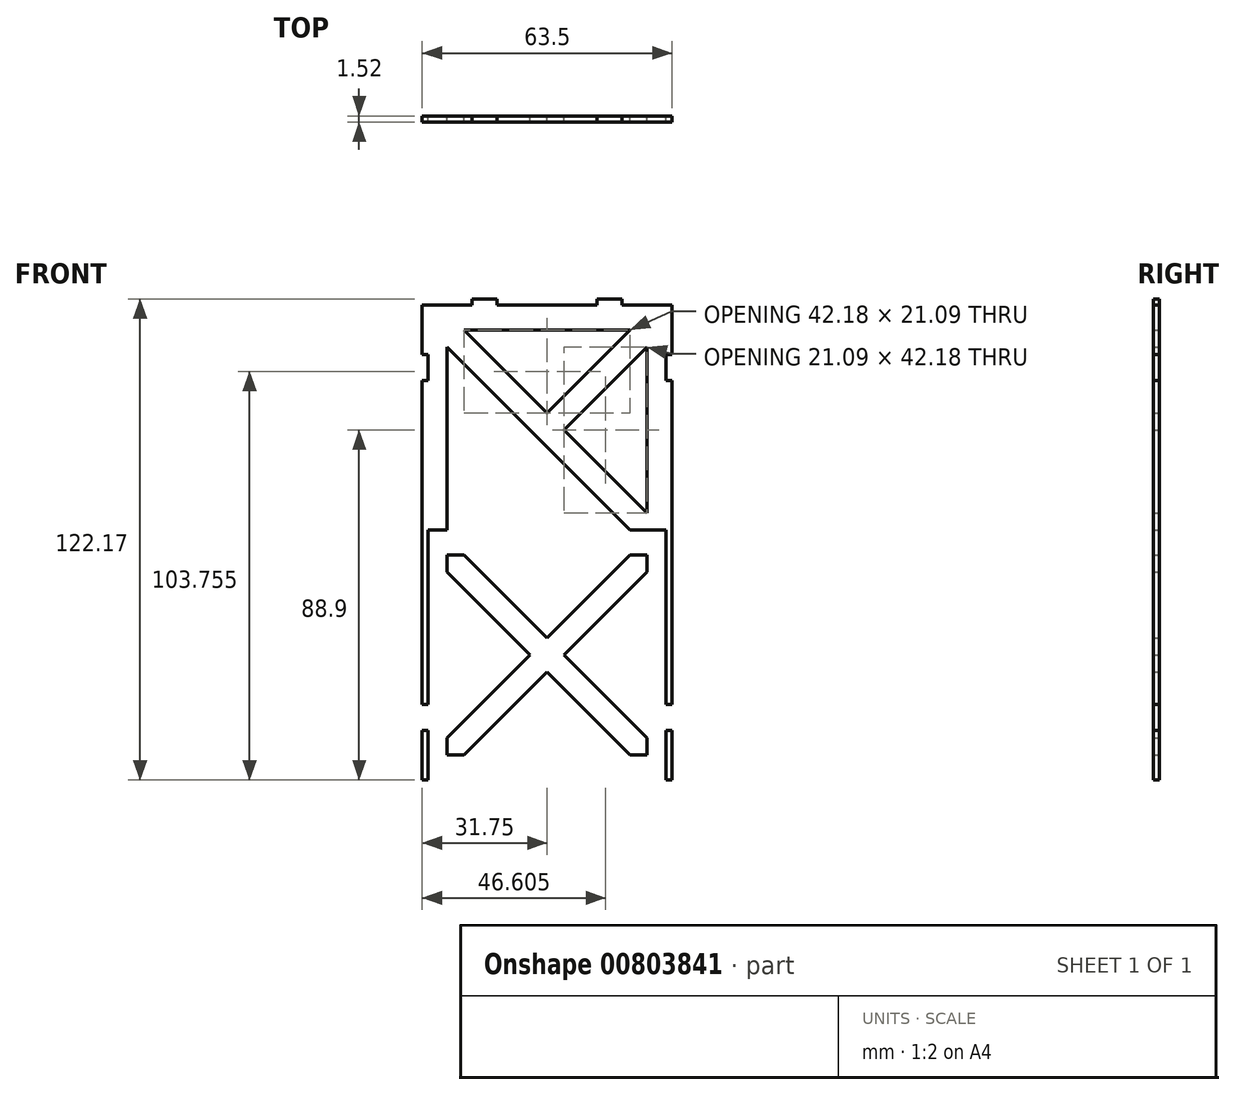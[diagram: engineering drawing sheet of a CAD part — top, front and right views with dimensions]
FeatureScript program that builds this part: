
annotation { "Feature Type Name" : "Feature", "Feature Type Description" : "" }
export const myFeature = defineFeature(function(context is Context, id is Id, definition is map)
    precondition{}
    {
        {
            var Q0;
            Q0=qCreatedBy(makeId("Front.planeOp"),FACE);
            var sketch = newSketch(context, id + "F0", { "sketchPlane" : qUnion([Q0])});
            skLineSegment(sketch, "E0.bottom", {"start": v(31.75, 31.75) * mm, "end": v(-31.75, 31.75) * mm});
            skLineSegment(sketch, "E0.top", {"start": v(31.75, -31.75) * mm, "end": v(-31.75, -31.75) * mm});
            skLineSegment(sketch, "E0.left", {"start": v(31.75, 31.75) * mm, "end": v(31.75, -31.75) * mm});
            skLineSegment(sketch, "E0.right", {"start": v(-31.75, 31.75) * mm, "end": v(-31.75, -31.75) * mm});
            skPoint(sketch, "E0.middle", {"position": v(0, 0) * mm});
            skLineSegment(sketch, "E1.bottom", {"start": v(-19.05, -31.75) * mm, "end": v(-12.7, -31.75) * mm});
            skLineSegment(sketch, "E1.top", {"start": v(-19.05, -33.27) * mm, "end": v(-12.7, -33.27) * mm});
            skLineSegment(sketch, "E1.left", {"start": v(-19.05, -31.75) * mm, "end": v(-19.05, -33.27) * mm});
            skLineSegment(sketch, "E1.right", {"start": v(-12.7, -31.75) * mm, "end": v(-12.7, -33.27) * mm});
            skPoint(sketch, "E2", {"position": v(-15.88, -31.75) * mm});
            skLineSegment(sketch, "E3.MirrorCS", {"start": v(19.05, -31.75) * mm, "end": v(12.7, -31.75) * mm});
            skPoint(sketch, "E4.MirrorP", {"position": v(15.88, -31.75) * mm});
            skLineSegment(sketch, "E5.MirrorCS", {"start": v(19.05, -33.27) * mm, "end": v(12.7, -33.27) * mm});
            skLineSegment(sketch, "E6.MirrorCS", {"start": v(12.7, -31.75) * mm, "end": v(12.7, -33.27) * mm});
            skLineSegment(sketch, "E7.MirrorCS", {"start": v(19.05, -31.75) * mm, "end": v(19.05, -33.27) * mm});
            skLineSegment(sketch, "E8.bottom", {"start": v(-31.75, -19.18) * mm, "end": v(-30.23, -19.18) * mm});
            skLineSegment(sketch, "E8.top", {"start": v(-31.75, -12.57) * mm, "end": v(-30.23, -12.57) * mm});
            skLineSegment(sketch, "E8.left", {"start": v(-31.75, -19.18) * mm, "end": v(-31.75, -12.57) * mm});
            skLineSegment(sketch, "E8.right", {"start": v(-30.23, -19.18) * mm, "end": v(-30.23, -12.57) * mm});
            skPoint(sketch, "E9", {"position": v(-31.75, -15.88) * mm});
            skLineSegment(sketch, "E10.MirrorCS", {"start": v(-31.75, 19.18) * mm, "end": v(-30.23, 19.18) * mm});
            skPoint(sketch, "E11.MirrorP", {"position": v(-31.75, 15.88) * mm});
            skLineSegment(sketch, "E12.MirrorCS", {"start": v(-31.75, 12.57) * mm, "end": v(-30.23, 12.57) * mm});
            skLineSegment(sketch, "E13.MirrorCS", {"start": v(-31.75, 19.18) * mm, "end": v(-31.75, 12.57) * mm});
            skLineSegment(sketch, "E14.MirrorCS", {"start": v(-30.23, 19.18) * mm, "end": v(-30.23, 12.57) * mm});
            skLineSegment(sketch, "E15.MirrorCS", {"start": v(31.75, 19.18) * mm, "end": v(30.23, 19.18) * mm});
            skLineSegment(sketch, "E16.MirrorCS", {"start": v(31.75, -19.18) * mm, "end": v(30.23, -19.18) * mm});
            skLineSegment(sketch, "E17.MirrorCS", {"start": v(31.75, -12.57) * mm, "end": v(30.23, -12.57) * mm});
            skLineSegment(sketch, "E18.MirrorCS", {"start": v(31.75, 12.57) * mm, "end": v(30.23, 12.57) * mm});
            skLineSegment(sketch, "E19.MirrorCS", {"start": v(30.23, 19.18) * mm, "end": v(30.23, 12.57) * mm});
            skLineSegment(sketch, "E20.MirrorCS", {"start": v(30.23, -19.18) * mm, "end": v(30.23, -12.57) * mm});
            skLineSegment(sketch, "E21.MirrorCS", {"start": v(31.75, 19.18) * mm, "end": v(31.75, 12.57) * mm});
            skLineSegment(sketch, "E22.MirrorCS", {"start": v(31.75, -19.18) * mm, "end": v(31.75, -12.57) * mm});
            skPoint(sketch, "E23.MirrorP", {"position": v(31.75, 15.88) * mm});
            skPoint(sketch, "E24.MirrorP", {"position": v(31.75, -15.88) * mm});
            skLineSegment(sketch, "E25.0", {"start": v(-30.23, 31.75) * mm, "end": v(-30.23, -31.75) * mm});
            skLineSegment(sketch, "E26.MirrorCS", {"start": v(30.23, 31.75) * mm, "end": v(30.23, -31.75) * mm});
            skLineSegment(sketch, "E27.bottom", {"start": v(25.4, 25.4) * mm, "end": v(-25.4, 25.4) * mm});
            skLineSegment(sketch, "E27.top", {"start": v(25.4, -25.4) * mm, "end": v(-25.4, -25.4) * mm});
            skLineSegment(sketch, "E27.left", {"start": v(25.4, 25.4) * mm, "end": v(25.4, -25.4) * mm});
            skLineSegment(sketch, "E27.right", {"start": v(-25.4, 25.4) * mm, "end": v(-25.4, -25.4) * mm});
            skLineSegment(sketch, "E28", {"start": v(-25.4, -25.4) * mm, "end": v(25.4, 25.4) * mm, "construction": true});
            skLineSegment(sketch, "E29", {"start": v(-25.4, 25.4) * mm, "end": v(25.4, -25.4) * mm, "construction": true});
            skLineSegment(sketch, "E30.0", {"start": v(-27.56, 23.24) * mm, "end": v(23.24, -27.56) * mm});
            skLineSegment(sketch, "E31.0", {"start": v(-23.24, 27.56) * mm, "end": v(27.56, -23.24) * mm});
            skLineSegment(sketch, "E32.0", {"start": v(-23.24, -27.56) * mm, "end": v(27.56, 23.24) * mm});
            skLineSegment(sketch, "E33.0", {"start": v(-27.56, -23.24) * mm, "end": v(23.24, 27.56) * mm});
            skLineSegment(sketch, "E34.MirrorCS", {"start": v(-19.05, 31.75) * mm, "end": v(-19.05, 33.27) * mm});
            skLineSegment(sketch, "E35.MirrorCS", {"start": v(-12.7, 31.75) * mm, "end": v(-12.7, 33.27) * mm});
            skLineSegment(sketch, "E36.MirrorCS", {"start": v(12.7, 31.75) * mm, "end": v(12.7, 33.27) * mm});
            skLineSegment(sketch, "E37.MirrorCS", {"start": v(19.05, 31.75) * mm, "end": v(19.05, 33.27) * mm});
            skLineSegment(sketch, "E38.MirrorCS", {"start": v(-19.05, 31.75) * mm, "end": v(-12.7, 31.75) * mm});
            skLineSegment(sketch, "E39.MirrorCS", {"start": v(-19.05, 33.27) * mm, "end": v(-12.7, 33.27) * mm});
            skLineSegment(sketch, "E40.MirrorCS", {"start": v(19.05, 31.75) * mm, "end": v(12.7, 31.75) * mm});
            skLineSegment(sketch, "E41.MirrorCS", {"start": v(19.05, 33.27) * mm, "end": v(12.7, 33.27) * mm});
            skPoint(sketch, "E42.MirrorP", {"position": v(-15.88, 31.75) * mm});
            skPoint(sketch, "E43.MirrorP", {"position": v(15.88, 31.75) * mm});
            skLineSegment(sketch, "E44", {"start": v(0, 31.75) * mm, "end": v(0, 25.4) * mm, "construction": true});
            skLineSegment(sketch, "E45", {"start": v(0, 28.58) * mm, "end": v(31.75, 28.58) * mm, "construction": true});
            skLineSegment(sketch, "E46.MirrorCS", {"start": v(-31.75, 76.33) * mm, "end": v(-30.23, 76.33) * mm});
            skLineSegment(sketch, "E47.MirrorCS", {"start": v(-12.7, 88.9) * mm, "end": v(-12.7, 90.42) * mm});
            skLineSegment(sketch, "E48.MirrorCS", {"start": v(12.7, 88.9) * mm, "end": v(12.7, 90.42) * mm});
            skLineSegment(sketch, "E49.MirrorCS", {"start": v(-31.75, 69.72) * mm, "end": v(-30.23, 69.72) * mm});
            skLineSegment(sketch, "E50.MirrorCS", {"start": v(-19.05, 88.9) * mm, "end": v(-19.05, 90.42) * mm});
            skLineSegment(sketch, "E51.MirrorCS", {"start": v(31.75, 76.33) * mm, "end": v(30.23, 76.33) * mm});
            skLineSegment(sketch, "E52.MirrorCS", {"start": v(19.05, 88.9) * mm, "end": v(19.05, 90.42) * mm});
            skLineSegment(sketch, "E53.MirrorCS", {"start": v(31.75, 69.72) * mm, "end": v(30.23, 69.72) * mm});
            skLineSegment(sketch, "E54.MirrorCS", {"start": v(12.7, 25.4) * mm, "end": v(12.7, 23.88) * mm});
            skLineSegment(sketch, "E55.MirrorCS", {"start": v(31.75, 44.58) * mm, "end": v(30.23, 44.58) * mm});
            skLineSegment(sketch, "E56.MirrorCS", {"start": v(-12.7, 25.4) * mm, "end": v(-12.7, 23.88) * mm});
            skLineSegment(sketch, "E57.MirrorCS", {"start": v(-31.75, 37.97) * mm, "end": v(-30.23, 37.97) * mm});
            skLineSegment(sketch, "E58.MirrorCS", {"start": v(-19.05, 25.4) * mm, "end": v(-19.05, 23.88) * mm});
            skLineSegment(sketch, "E59.MirrorCS", {"start": v(-31.75, 44.58) * mm, "end": v(-30.23, 44.58) * mm});
            skLineSegment(sketch, "E60.MirrorCS", {"start": v(31.75, 37.97) * mm, "end": v(30.23, 37.97) * mm});
            skLineSegment(sketch, "E61.MirrorCS", {"start": v(19.05, 25.4) * mm, "end": v(19.05, 23.88) * mm});
            skLineSegment(sketch, "E62.MirrorCS", {"start": v(-19.05, 90.42) * mm, "end": v(-12.7, 90.42) * mm});
            skLineSegment(sketch, "E63.MirrorCS", {"start": v(-19.05, 25.4) * mm, "end": v(-12.7, 25.4) * mm});
            skLineSegment(sketch, "E64.MirrorCS", {"start": v(19.05, 25.4) * mm, "end": v(12.7, 25.4) * mm});
            skLineSegment(sketch, "E65.MirrorCS", {"start": v(19.05, 88.9) * mm, "end": v(12.7, 88.9) * mm});
            skLineSegment(sketch, "E66.MirrorCS", {"start": v(19.05, 90.42) * mm, "end": v(12.7, 90.42) * mm});
            skLineSegment(sketch, "E67.MirrorCS", {"start": v(-31.75, 76.33) * mm, "end": v(-31.75, 69.72) * mm});
            skLineSegment(sketch, "E68.MirrorCS", {"start": v(-30.23, 76.33) * mm, "end": v(-30.23, 69.72) * mm});
            skLineSegment(sketch, "E69.MirrorCS", {"start": v(-19.05, 88.9) * mm, "end": v(-12.7, 88.9) * mm});
            skLineSegment(sketch, "E70.MirrorCS", {"start": v(19.05, 23.88) * mm, "end": v(12.7, 23.88) * mm});
            skLineSegment(sketch, "E71.MirrorCS", {"start": v(31.75, 37.97) * mm, "end": v(31.75, 44.58) * mm});
            skLineSegment(sketch, "E72.MirrorCS", {"start": v(-19.05, 23.88) * mm, "end": v(-12.7, 23.88) * mm});
            skLineSegment(sketch, "E73.MirrorCS", {"start": v(30.23, 76.33) * mm, "end": v(30.23, 69.72) * mm});
            skLineSegment(sketch, "E74.MirrorCS", {"start": v(-31.75, 37.97) * mm, "end": v(-31.75, 44.58) * mm});
            skLineSegment(sketch, "E75.MirrorCS", {"start": v(-30.23, 37.97) * mm, "end": v(-30.23, 44.58) * mm});
            skLineSegment(sketch, "E76.MirrorCS", {"start": v(31.75, 76.33) * mm, "end": v(31.75, 69.72) * mm});
            skLineSegment(sketch, "E77.MirrorCS", {"start": v(30.23, 37.97) * mm, "end": v(30.23, 44.58) * mm});
            skPoint(sketch, "E78.MirrorP", {"position": v(0, 57.15) * mm});
            skLineSegment(sketch, "E79.MirrorCS", {"start": v(0, 25.4) * mm, "end": v(0, 31.75) * mm, "construction": true});
            skLineSegment(sketch, "E80.MirrorCS", {"start": v(31.75, 25.4) * mm, "end": v(-31.75, 25.4) * mm});
            skLineSegment(sketch, "E81.MirrorCS", {"start": v(31.75, 25.4) * mm, "end": v(31.75, 88.9) * mm});
            skPoint(sketch, "E82.MirrorP", {"position": v(-15.88, 25.4) * mm});
            skLineSegment(sketch, "E83.MirrorCS", {"start": v(25.4, 31.75) * mm, "end": v(-25.4, 31.75) * mm});
            skLineSegment(sketch, "E84.MirrorCS", {"start": v(-23.24, 29.6) * mm, "end": v(27.56, 80.4) * mm});
            skPoint(sketch, "E85.MirrorP", {"position": v(15.87, 88.9) * mm});
            skPoint(sketch, "E86.MirrorP", {"position": v(-15.88, 88.9) * mm});
            skLineSegment(sketch, "E87.MirrorCS", {"start": v(31.75, 88.9) * mm, "end": v(-31.75, 88.9) * mm});
            skLineSegment(sketch, "E88.MirrorCS", {"start": v(-31.75, 25.4) * mm, "end": v(-31.75, 88.9) * mm});
            skLineSegment(sketch, "E89.MirrorCS", {"start": v(-30.23, 25.4) * mm, "end": v(-30.23, 88.9) * mm});
            skLineSegment(sketch, "E90.MirrorCS", {"start": v(25.4, 82.55) * mm, "end": v(-25.4, 82.55) * mm});
            skLineSegment(sketch, "E91.MirrorCS", {"start": v(-23.24, 84.7) * mm, "end": v(27.56, 33.9) * mm});
            skLineSegment(sketch, "E92.MirrorCS", {"start": v(-27.56, 33.9) * mm, "end": v(23.24, 84.7) * mm});
            skLineSegment(sketch, "E93.MirrorCS", {"start": v(25.4, 31.75) * mm, "end": v(25.4, 82.55) * mm});
            skLineSegment(sketch, "E94.MirrorCS", {"start": v(30.23, 25.4) * mm, "end": v(30.23, 88.9) * mm});
            skLineSegment(sketch, "E95.MirrorCS", {"start": v(-27.56, 80.4) * mm, "end": v(23.24, 29.6) * mm});
            skPoint(sketch, "E96.MirrorP", {"position": v(-31.75, 73.03) * mm});
            skPoint(sketch, "E97.MirrorP", {"position": v(15.88, 25.4) * mm});
            skPoint(sketch, "E98.MirrorP", {"position": v(31.75, 41.28) * mm});
            skLineSegment(sketch, "E99.MirrorCS", {"start": v(-25.4, 82.55) * mm, "end": v(25.4, 31.75) * mm, "construction": true});
            skPoint(sketch, "E100.MirrorP", {"position": v(31.75, 73.03) * mm});
            skPoint(sketch, "E101.MirrorP", {"position": v(-31.75, 41.27) * mm});
            skLineSegment(sketch, "E102.MirrorCS", {"start": v(-25.4, 31.75) * mm, "end": v(25.4, 82.55) * mm, "construction": true});
            skLineSegment(sketch, "E103.MirrorCS", {"start": v(-25.4, 31.75) * mm, "end": v(-25.4, 82.55) * mm});
            skSolve(sketch);
        }
        {
            var Q0;
            {var subQ0=sQuery(id+"F0.wireOp",EDGE,"E8.top");Q0=makeQuery(id+"F0.imprint","IMPRINT",FACE,{"disambiguationData":[TD([[makeQuery(id+"F0.imprint","IMPRINT",EDGE,{"derivedFrom":subQ0}),1.0]])]});}
            var Q1;
            {var subQ5=sQuery(id+"F0.wireOp",EDGE,"E8.bottom");Q1=makeQuery(id+"F0.imprint","IMPRINT",FACE,{"disambiguationData":[TD([[makeQuery(id+"F0.imprint","IMPRINT",EDGE,{"derivedFrom":subQ5}),-1.0]])]});}
            var Q2;
            {var subQ21=sQuery(id+"F0.wireOp",EDGE,"E1.bottom");Q2=makeQuery(id+"F0.imprint","IMPRINT",FACE,{"disambiguationData":[TD([[makeQuery(id+"F0.imprint","IMPRINT",EDGE,{"derivedFrom":subQ21}),1.0]])]});}
            var Q3;
            {var subQ1=sQuery(id+"F0.wireOp",EDGE,"E27.top");var subQ7=sQuery(id+"F0.wireOp",EDGE,"E27.right");var subQ8=makeQuery(id+"F0.imprint","INTERSECT",VERTEX,{"derivedFrom":[subQ1,subQ7]});Q3=makeQuery(id+"F0.imprint","IMPRINT",FACE,{"disambiguationData":[TD([[makeQuery(id+"F0.imprint","IMPRINT",EDGE,{"disambiguationData":[TD([[subQ8,1.0]])],"derivedFrom":subQ1}),-1.0]])]});}
            var Q4;
            {var subQ1=sQuery(id+"F0.wireOp",EDGE,"E27.left");var subQ6=sQuery(id+"F0.wireOp",EDGE,"E27.top");var subQ9=makeQuery(id+"F0.imprint","INTERSECT",VERTEX,{"derivedFrom":[subQ6,subQ1]});Q4=makeQuery(id+"F0.imprint","IMPRINT",FACE,{"disambiguationData":[TD([[makeQuery(id+"F0.imprint","IMPRINT",EDGE,{"disambiguationData":[TD([[subQ9,-1.0]])],"derivedFrom":subQ6}),-1.0]])]});}
            var Q5;
            {var subQ0=sQuery(id+"F0.wireOp",EDGE,"E33.0");var subQ1=sQuery(id+"F0.wireOp",EDGE,"E30.0");var subQ2=makeQuery(id+"F0.imprint","INTERSECT",VERTEX,{"derivedFrom":[subQ1,subQ0]});Q5=makeQuery(id+"F0.imprint","IMPRINT",FACE,{"disambiguationData":[TD([[makeQuery(id+"F0.imprint","IMPRINT",EDGE,{"disambiguationData":[TD([[subQ2,-1.0]])],"derivedFrom":subQ1}),1.0]])]});}
            var Q6;
            {var subQ0=sQuery(id+"F0.wireOp",EDGE,"E80.MirrorCS");var subQ6=sQuery(id+"F0.wireOp",EDGE,"E27.left");var subQ9=makeQuery(id+"F0.imprint","INTERSECT",VERTEX,{"derivedFrom":[subQ6,subQ0]});Q6=makeQuery(id+"F0.imprint","IMPRINT",FACE,{"disambiguationData":[TD([[makeQuery(id+"F0.imprint","IMPRINT",EDGE,{"disambiguationData":[TD([[subQ9,-1.0]])],"derivedFrom":subQ6}),-1.0]])]});}
            var Q7;
            {var subQ0=sQuery(id+"F0.wireOp",EDGE,"E80.MirrorCS");var subQ7=sQuery(id+"F0.wireOp",EDGE,"E27.right");var subQ9=makeQuery(id+"F0.imprint","INTERSECT",VERTEX,{"derivedFrom":[subQ7,subQ0]});Q7=makeQuery(id+"F0.imprint","IMPRINT",FACE,{"disambiguationData":[TD([[makeQuery(id+"F0.imprint","IMPRINT",EDGE,{"disambiguationData":[TD([[subQ9,-1.0]])],"derivedFrom":subQ7}),1.0]])]});}
            var Q8;
            Q8=makeQuery(id+"F0.imprint","IMPRINT",FACE,{"disambiguationData":[TD([[makeQuery(id+"F0.imprint","IMPRINT",EDGE,{"derivedFrom":sQuery(id+"F0.wireOp",EDGE,"E3.MirrorCS")}),1.0]])]});
            var Q9;
            Q9=makeQuery(id+"F0.imprint","IMPRINT",FACE,{"disambiguationData":[TD([[makeQuery(id+"F0.imprint","IMPRINT",EDGE,{"derivedFrom":sQuery(id+"F0.wireOp",EDGE,"E1.bottom")}),-1.0]])]});
            var Q10;
            {var subQ0=sQuery(id+"F0.wireOp",EDGE,"E80.MirrorCS");var subQ14=makeQuery(id+"F0.imprint","INTERSECT",VERTEX,{"derivedFrom":[sQuery(id+"F0.wireOp",EDGE,"E27.left"),subQ0]});Q10=makeQuery(id+"F0.imprint","IMPRINT",FACE,{"disambiguationData":[TD([[makeQuery(id+"F0.imprint","IMPRINT",EDGE,{"disambiguationData":[TD([[subQ14,-1.0]])],"derivedFrom":subQ0}),-1.0]])]});}
            var Q11;
            {var subQ1=sQuery(id+"F0.wireOp",EDGE,"E84.MirrorCS");var subQ7=sQuery(id+"F0.wireOp",EDGE,"E83.MirrorCS");var subQ8=makeQuery(id+"F0.imprint","INTERSECT",VERTEX,{"derivedFrom":[subQ7,subQ1]});Q11=makeQuery(id+"F0.imprint","IMPRINT",FACE,{"disambiguationData":[TD([[makeQuery(id+"F0.imprint","IMPRINT",EDGE,{"disambiguationData":[TD([[subQ8,-1.0]])],"derivedFrom":subQ1}),1.0]])]});}
            var Q12;
            {var subQ0=sQuery(id+"F0.wireOp",EDGE,"E95.MirrorCS");var subQ1=sQuery(id+"F0.wireOp",EDGE,"E84.MirrorCS");var subQ2=makeQuery(id+"F0.imprint","INTERSECT",VERTEX,{"derivedFrom":[subQ1,subQ0]});Q12=makeQuery(id+"F0.imprint","IMPRINT",FACE,{"disambiguationData":[TD([[makeQuery(id+"F0.imprint","IMPRINT",EDGE,{"disambiguationData":[TD([[subQ2,-1.0]])],"derivedFrom":subQ1}),1.0]])]});}
            var Q13;
            {var subQ3=sQuery(id+"F0.wireOp",EDGE,"E84.MirrorCS");var subQ7=sQuery(id+"F0.wireOp",EDGE,"E95.MirrorCS");var subQ9=makeQuery(id+"F0.imprint","INTERSECT",VERTEX,{"derivedFrom":[subQ3,subQ7]});Q13=makeQuery(id+"F0.imprint","IMPRINT",FACE,{"disambiguationData":[TD([[makeQuery(id+"F0.imprint","IMPRINT",EDGE,{"disambiguationData":[TD([[subQ9,-1.0]])],"derivedFrom":subQ3}),-1.0]])]});}
            var Q14;
            {var subQ3=sQuery(id+"F0.wireOp",EDGE,"E10.MirrorCS");Q14=makeQuery(id+"F0.imprint","IMPRINT",FACE,{"disambiguationData":[TD([[makeQuery(id+"F0.imprint","IMPRINT",EDGE,{"derivedFrom":subQ3}),1.0]])]});}
            var Q15;
            {var subQ0=sQuery(id+"F0.wireOp",EDGE,"E88.MirrorCS");var subQ1=sQuery(id+"F0.wireOp",EDGE,"E0.bottom");var subQ2=makeQuery(id+"F0.imprint","INTERSECT",VERTEX,{"derivedFrom":[subQ1,subQ0]});Q15=makeQuery(id+"F0.imprint","IMPRINT",FACE,{"disambiguationData":[TD([[makeQuery(id+"F0.imprint","IMPRINT",EDGE,{"disambiguationData":[TD([[subQ2,1.0]])],"derivedFrom":subQ1}),1.0]])]});}
            var Q16;
            {var subQ5=sQuery(id+"F0.wireOp",EDGE,"E57.MirrorCS");Q16=makeQuery(id+"F0.imprint","IMPRINT",FACE,{"disambiguationData":[TD([[makeQuery(id+"F0.imprint","IMPRINT",EDGE,{"derivedFrom":subQ5}),-1.0]])]});}
            var Q17;
            {var subQ0=sQuery(id+"F0.wireOp",EDGE,"E10.MirrorCS");Q17=makeQuery(id+"F0.imprint","IMPRINT",FACE,{"disambiguationData":[TD([[makeQuery(id+"F0.imprint","IMPRINT",EDGE,{"derivedFrom":subQ0}),-1.0]])]});}
            var Q18;
            {var subQ0=sQuery(id+"F0.wireOp",EDGE,"E57.MirrorCS");Q18=makeQuery(id+"F0.imprint","IMPRINT",FACE,{"disambiguationData":[TD([[makeQuery(id+"F0.imprint","IMPRINT",EDGE,{"derivedFrom":subQ0}),1.0]])]});}
            var Q19;
            {var subQ17=sQuery(id+"F0.wireOp",EDGE,"E87.MirrorCS");var subQ20=makeQuery(id+"F0.imprint","INTERSECT",VERTEX,{"derivedFrom":[sQuery(id+"F0.wireOp",EDGE,"E52.MirrorCS"),subQ17]});Q19=makeQuery(id+"F0.imprint","IMPRINT",FACE,{"disambiguationData":[TD([[makeQuery(id+"F0.imprint","IMPRINT",EDGE,{"disambiguationData":[TD([[subQ20,1.0]])],"derivedFrom":subQ17}),1.0]])]});}
            var Q20;
            {var subQ0=sQuery(id+"F0.wireOp",EDGE,"E17.MirrorCS");Q20=makeQuery(id+"F0.imprint","IMPRINT",FACE,{"disambiguationData":[TD([[makeQuery(id+"F0.imprint","IMPRINT",EDGE,{"derivedFrom":subQ0}),-1.0]])]});}
            var Q21;
            {var subQ5=sQuery(id+"F0.wireOp",EDGE,"E16.MirrorCS");Q21=makeQuery(id+"F0.imprint","IMPRINT",FACE,{"disambiguationData":[TD([[makeQuery(id+"F0.imprint","IMPRINT",EDGE,{"derivedFrom":subQ5}),1.0]])]});}
            var Q22;
            {var subQ3=sQuery(id+"F0.wireOp",EDGE,"E15.MirrorCS");Q22=makeQuery(id+"F0.imprint","IMPRINT",FACE,{"disambiguationData":[TD([[makeQuery(id+"F0.imprint","IMPRINT",EDGE,{"derivedFrom":subQ3}),-1.0]])]});}
            var Q23;
            {var subQ0=sQuery(id+"F0.wireOp",EDGE,"E81.MirrorCS");var subQ1=sQuery(id+"F0.wireOp",EDGE,"E0.bottom");var subQ2=makeQuery(id+"F0.imprint","INTERSECT",VERTEX,{"derivedFrom":[subQ1,subQ0]});Q23=makeQuery(id+"F0.imprint","IMPRINT",FACE,{"disambiguationData":[TD([[makeQuery(id+"F0.imprint","IMPRINT",EDGE,{"disambiguationData":[TD([[subQ2,-1.0]])],"derivedFrom":subQ1}),1.0]])]});}
            var Q24;
            {var subQ5=sQuery(id+"F0.wireOp",EDGE,"E60.MirrorCS");Q24=makeQuery(id+"F0.imprint","IMPRINT",FACE,{"disambiguationData":[TD([[makeQuery(id+"F0.imprint","IMPRINT",EDGE,{"derivedFrom":subQ5}),1.0]])]});}
            var Q25;
            {var subQ0=sQuery(id+"F0.wireOp",EDGE,"E55.MirrorCS");Q25=makeQuery(id+"F0.imprint","IMPRINT",FACE,{"disambiguationData":[TD([[makeQuery(id+"F0.imprint","IMPRINT",EDGE,{"derivedFrom":subQ0}),1.0]])]});}
            var Q26;
            {var subQ0=sQuery(id+"F0.wireOp",EDGE,"E53.MirrorCS");Q26=makeQuery(id+"F0.imprint","IMPRINT",FACE,{"disambiguationData":[TD([[makeQuery(id+"F0.imprint","IMPRINT",EDGE,{"derivedFrom":subQ0}),1.0]])]});}
            var Q27;
            {var subQ5=sQuery(id+"F0.wireOp",EDGE,"E84.MirrorCS");var subQ7=sQuery(id+"F0.wireOp",EDGE,"E93.MirrorCS");var subQ9=makeQuery(id+"F0.imprint","INTERSECT",VERTEX,{"derivedFrom":[subQ5,subQ7]});Q27=makeQuery(id+"F0.imprint","IMPRINT",FACE,{"disambiguationData":[TD([[makeQuery(id+"F0.imprint","IMPRINT",EDGE,{"disambiguationData":[TD([[subQ9,1.0]])],"derivedFrom":subQ5}),1.0]])]});}
            var Q28;
            {var subQ0=sQuery(id+"F0.wireOp",EDGE,"E103.MirrorCS");var subQ7=sQuery(id+"F0.wireOp",EDGE,"E90.MirrorCS");var subQ9=makeQuery(id+"F0.imprint","INTERSECT",VERTEX,{"derivedFrom":[subQ7,subQ0]});Q28=makeQuery(id+"F0.imprint","IMPRINT",FACE,{"disambiguationData":[TD([[makeQuery(id+"F0.imprint","IMPRINT",EDGE,{"disambiguationData":[TD([[subQ9,1.0]])],"derivedFrom":subQ7}),1.0]])]});}
            var Q29;
            {var subQ0=sQuery(id+"F0.wireOp",EDGE,"E49.MirrorCS");Q29=makeQuery(id+"F0.imprint","IMPRINT",FACE,{"disambiguationData":[TD([[makeQuery(id+"F0.imprint","IMPRINT",EDGE,{"derivedFrom":subQ0}),-1.0]])]});}
            var Q30;
            {var subQ0=sQuery(id+"F0.wireOp",EDGE,"E46.MirrorCS");Q30=makeQuery(id+"F0.imprint","IMPRINT",FACE,{"disambiguationData":[TD([[makeQuery(id+"F0.imprint","IMPRINT",EDGE,{"derivedFrom":subQ0}),1.0]])]});}
            var Q31;
            {var subQ0=sQuery(id+"F0.wireOp",EDGE,"E51.MirrorCS");Q31=makeQuery(id+"F0.imprint","IMPRINT",FACE,{"disambiguationData":[TD([[makeQuery(id+"F0.imprint","IMPRINT",EDGE,{"derivedFrom":subQ0}),-1.0]])]});}
            var Q32;
            {var subQ0=sQuery(id+"F0.wireOp",EDGE,"E15.MirrorCS");Q32=makeQuery(id+"F0.imprint","IMPRINT",FACE,{"disambiguationData":[TD([[makeQuery(id+"F0.imprint","IMPRINT",EDGE,{"derivedFrom":subQ0}),1.0]])]});}
            var Q33;
            {var subQ0=sQuery(id+"F0.wireOp",EDGE,"E48.MirrorCS");Q33=makeQuery(id+"F0.imprint","IMPRINT",FACE,{"disambiguationData":[TD([[makeQuery(id+"F0.imprint","IMPRINT",EDGE,{"derivedFrom":subQ0}),-1.0]])]});}
            var Q34;
            {var subQ0=sQuery(id+"F0.wireOp",EDGE,"E47.MirrorCS");Q34=makeQuery(id+"F0.imprint","IMPRINT",FACE,{"disambiguationData":[TD([[makeQuery(id+"F0.imprint","IMPRINT",EDGE,{"derivedFrom":subQ0}),1.0]])]});}
            extrude(context, id + "F1", {"entities" : qUnion([Q0, Q1, Q2, Q3, Q4, Q5, Q6, Q7, Q8, Q9, Q10, Q11, Q12, Q13, Q14, Q15, Q16, Q17, Q18, Q19, Q20, Q21, Q22, Q23, Q24, Q25, Q26, Q27, Q28, Q29, Q30, Q31, Q32, Q33, Q34]), "depth" : 1.52 * mm, "offsetDistance" : 25.4 * mm});
        }
    });
